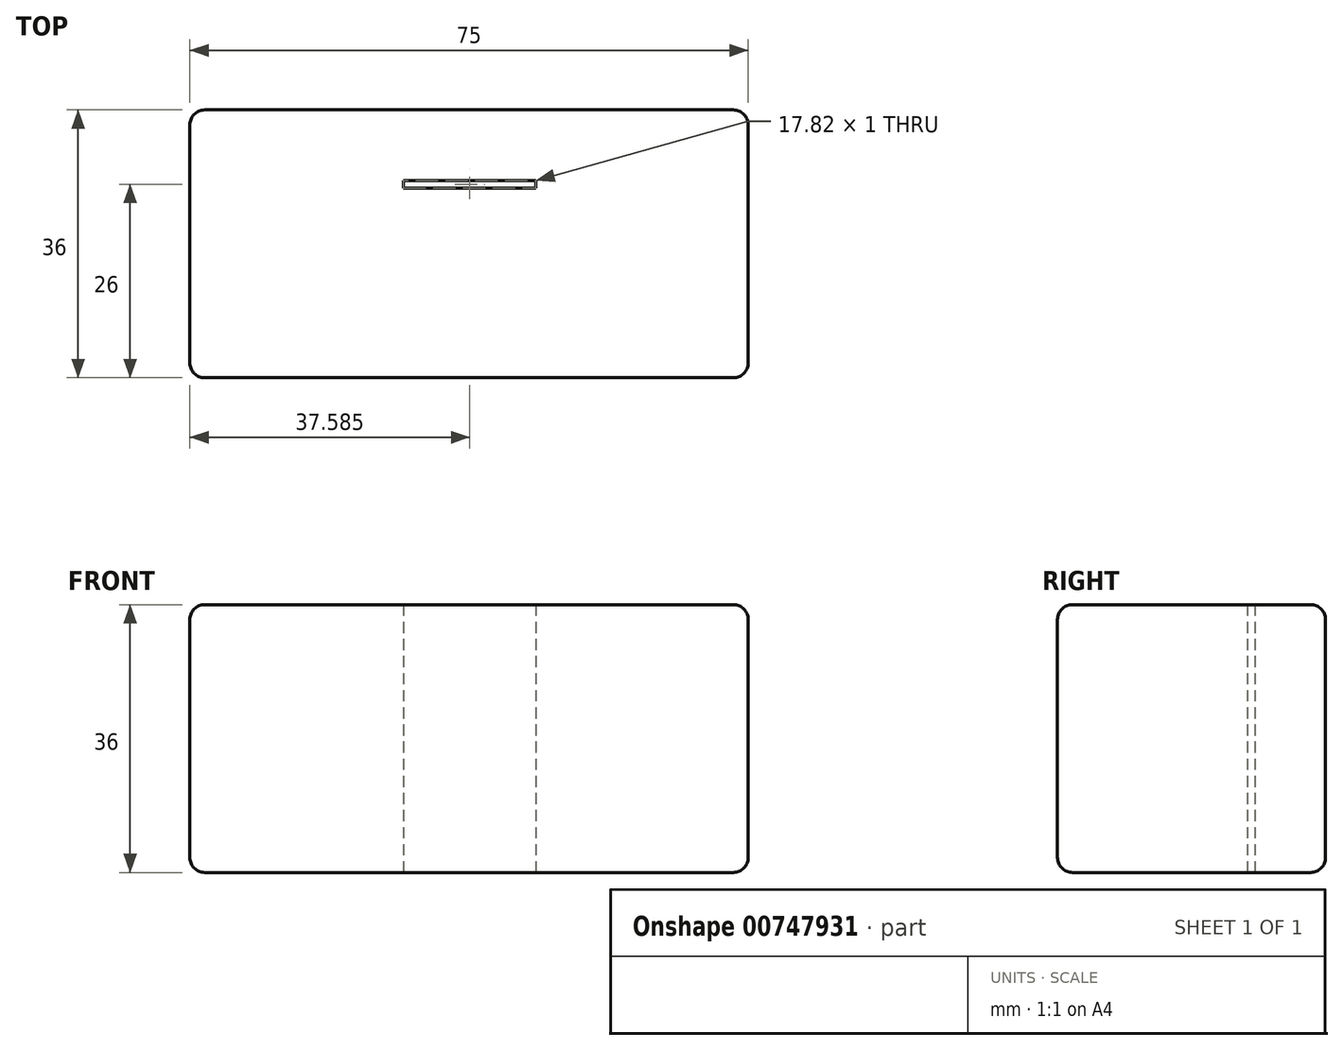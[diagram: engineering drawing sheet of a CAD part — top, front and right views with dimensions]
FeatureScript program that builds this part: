
annotation { "Feature Type Name" : "Feature", "Feature Type Description" : "" }
export const myFeature = defineFeature(function(context is Context, id is Id, definition is map)
    precondition{}
    {
        {
            var Q0;
            Q0=qCreatedBy(makeId("Top.planeOp"),FACE);
            var sketch = newSketch(context, id + "F0", { "sketchPlane" : qUnion([Q0])});
            skLineSegment(sketch, "E0.bottom", {"start": v(37.5, -18) * mm, "end": v(-37.5, -18) * mm});
            skLineSegment(sketch, "E0.top", {"start": v(37.5, 18) * mm, "end": v(-37.5, 18) * mm});
            skLineSegment(sketch, "E0.left", {"start": v(37.5, -18) * mm, "end": v(37.5, 18) * mm});
            skLineSegment(sketch, "E0.right", {"start": v(-37.5, -18) * mm, "end": v(-37.5, 18) * mm});
            skPoint(sketch, "E0.middle", {"position": v(0, 0) * mm});
            skLineSegment(sketch, "E1", {"start": v(-8.83, 8) * mm, "end": v(9, 8) * mm});
            skLineSegment(sketch, "E2.bottom", {"start": v(-8.83, 8.5) * mm, "end": v(9, 8.5) * mm});
            skLineSegment(sketch, "E2.top", {"start": v(-8.83, 7.5) * mm, "end": v(9, 7.5) * mm});
            skLineSegment(sketch, "E2.left", {"start": v(-8.83, 8.5) * mm, "end": v(-8.83, 7.5) * mm});
            skLineSegment(sketch, "E2.right", {"start": v(9, 8.5) * mm, "end": v(9, 7.5) * mm});
            skPoint(sketch, "E2.middle", {"position": v(0.09, 8) * mm});
            skSolve(sketch);
        }
        {
            var Q0;
            Q0 = qSketchRegion(id + "F0", true);
            extrude(context, id + "F1", {"entities" : qUnion([Q0]), "depth" : 36 * mm, "offsetDistance" : 25 * mm});
        }
        {
            var Q0;
            Q0=makeQuery(id+"F1.opExtrude","CAP_EDGE",EDGE,{"disambiguationData":[OSD([sQuery(id+"F0.wireOp",EDGE,"E0.bottom")])],"isStart":false});
            var Q1;
            Q1=makeQuery(id+"F1.opExtrude","SWEPT_EDGE",EDGE,{"disambiguationData":[OSD([sQuery(id+"F0.wireOp",EDGE,"E0.bottom"),sQuery(id+"F0.wireOp",EDGE,"E0.left")])]});
            var Q2;
            Q2=makeQuery(id+"F1.opExtrude","CAP_EDGE",EDGE,{"disambiguationData":[OSD([sQuery(id+"F0.wireOp",EDGE,"E0.left")])],"isStart":false});
            var Q3;
            Q3=makeQuery(id+"F1.opExtrude","SWEPT_EDGE",EDGE,{"disambiguationData":[OSD([sQuery(id+"F0.wireOp",EDGE,"E0.top"),sQuery(id+"F0.wireOp",EDGE,"E0.left")])]});
            var Q4;
            Q4=makeQuery(id+"F1.opExtrude","CAP_EDGE",EDGE,{"disambiguationData":[OSD([sQuery(id+"F0.wireOp",EDGE,"E0.left")])],"isStart":true});
            var Q5;
            Q5=makeQuery(id+"F1.opExtrude","CAP_EDGE",EDGE,{"disambiguationData":[OSD([sQuery(id+"F0.wireOp",EDGE,"E0.bottom")])],"isStart":true});
            var Q6;
            Q6=makeQuery(id+"F1.opExtrude","SWEPT_EDGE",EDGE,{"disambiguationData":[OSD([sQuery(id+"F0.wireOp",EDGE,"E0.bottom"),sQuery(id+"F0.wireOp",EDGE,"E0.right")])]});
            var Q7;
            Q7=makeQuery(id+"F1.opExtrude","CAP_EDGE",EDGE,{"disambiguationData":[OSD([sQuery(id+"F0.wireOp",EDGE,"E0.top")])],"isStart":true});
            var Q8;
            Q8=makeQuery(id+"F1.opExtrude","CAP_EDGE",EDGE,{"disambiguationData":[OSD([sQuery(id+"F0.wireOp",EDGE,"E0.right")])],"isStart":true});
            var Q9;
            Q9=makeQuery(id+"F1.opExtrude","SWEPT_EDGE",EDGE,{"disambiguationData":[OSD([sQuery(id+"F0.wireOp",EDGE,"E0.top"),sQuery(id+"F0.wireOp",EDGE,"E0.right")])]});
            var Q10;
            Q10=makeQuery(id+"F1.opExtrude","CAP_EDGE",EDGE,{"disambiguationData":[OSD([sQuery(id+"F0.wireOp",EDGE,"E0.right")])],"isStart":false});
            var Q11;
            Q11=makeQuery(id+"F1.opExtrude","CAP_EDGE",EDGE,{"disambiguationData":[OSD([sQuery(id+"F0.wireOp",EDGE,"E0.top")])],"isStart":false});
            fillet(context, id + "F2", {"entities" : qUnion([Q0, Q1, Q2, Q3, Q4, Q5, Q6, Q7, Q8, Q9, Q10, Q11]), "radius" : 2 * mm, "tangentPropagation" : true, "allowEdgeOverflow" : false});
        }
    });
